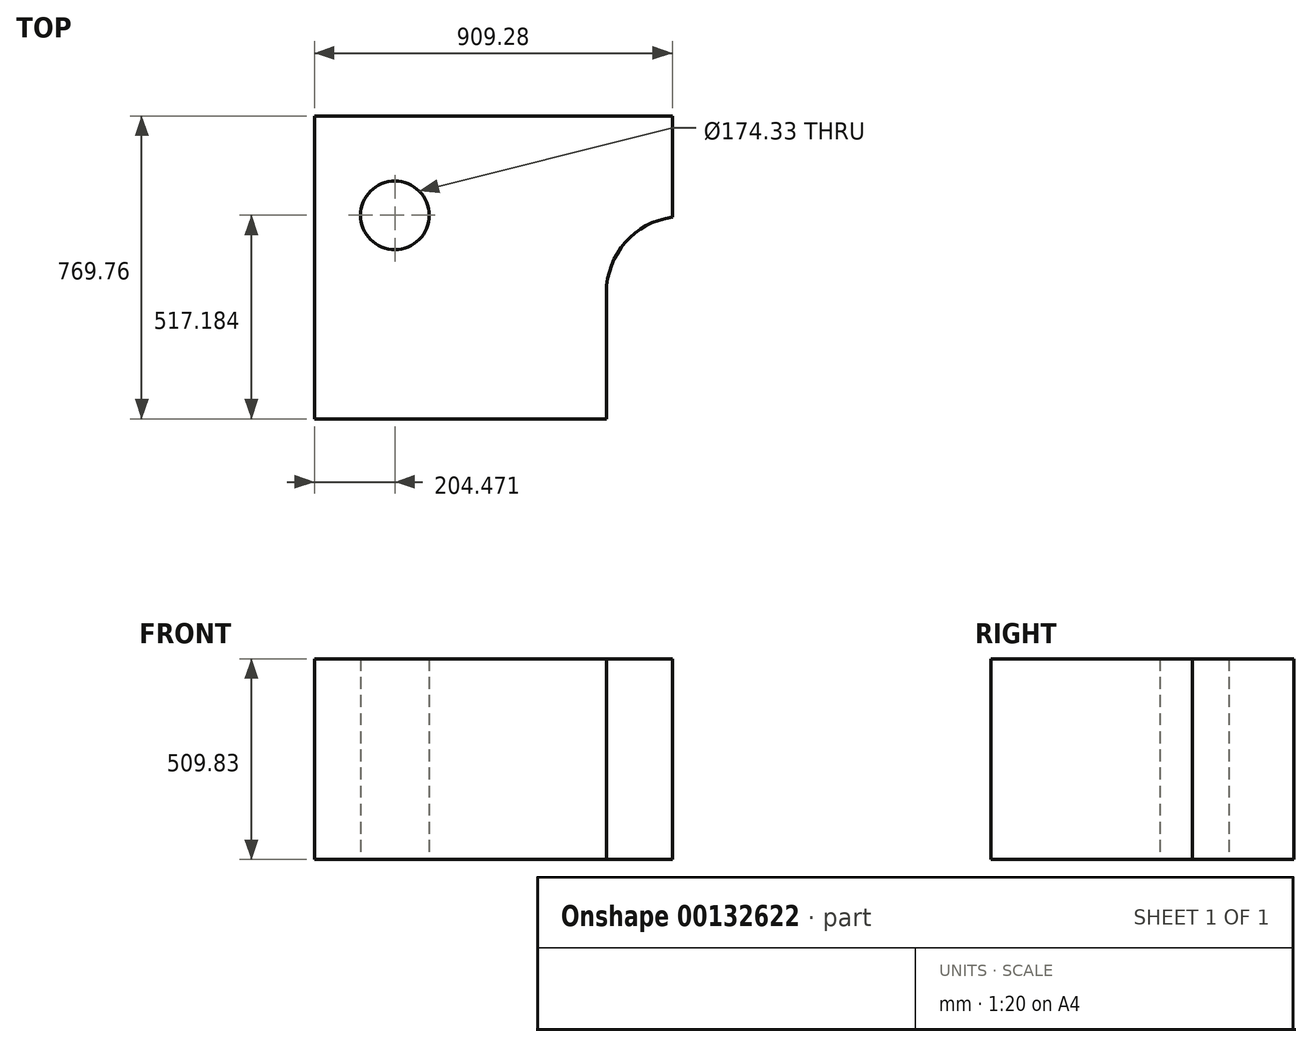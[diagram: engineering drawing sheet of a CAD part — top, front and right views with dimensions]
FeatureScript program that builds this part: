
annotation { "Feature Type Name" : "Feature", "Feature Type Description" : "" }
export const myFeature = defineFeature(function(context is Context, id is Id, definition is map)
    precondition{}
    {
        {
            var Q0;
            Q0=qCreatedBy(makeId("Top.planeOp"),FACE);
            var sketch = newSketch(context, id + "F0", { "sketchPlane" : qUnion([Q0])});
            skLineSegment(sketch, "E0.bottom", {"start": v(-645.88, 306.7) * mm, "end": v(263.4, 306.7) * mm});
            skLineSegment(sketch, "E0.top", {"start": v(-645.88, -463.06) * mm, "end": v(263.4, -463.06) * mm});
            skLineSegment(sketch, "E0.left", {"start": v(-645.88, 306.7) * mm, "end": v(-645.88, -463.06) * mm});
            skLineSegment(sketch, "E0.right", {"start": v(263.4, 306.7) * mm, "end": v(263.4, -463.06) * mm});
            skCircle(sketch, "E1", {"center": v(-441.4, 54.12) * mm, "radius": 87.16 * mm});
            skSolve(sketch);
        }
        {
            var Q0;
            Q0 = qSketchRegion(id + "F0", true);
            extrude(context, id + "F1", {"entities" : qUnion([Q0]), "depth" : 509.83 * mm});
        }
        {
            var Q0;
            Q0=makeQuery(id+"F1.opExtrude","SWEPT_FACE",FACE,{"disambiguationData":[OSD([sQuery(id+"F0.wireOp",EDGE,"E0.right")])]});
            var sketch = newSketch(context, id + "F2", { "sketchPlane" : qUnion([Q0])});
            skLineSegment(sketch, "E2.bottom", {"start": v(-463.06, 509.83) * mm, "end": v(49.12, 509.83) * mm});
            skLineSegment(sketch, "E2.top", {"start": v(-463.06, 0) * mm, "end": v(49.12, 0) * mm});
            skLineSegment(sketch, "E2.left", {"start": v(-463.06, 509.83) * mm, "end": v(-463.06, 0) * mm});
            skLineSegment(sketch, "E2.right", {"start": v(49.12, 509.83) * mm, "end": v(49.12, 0) * mm});
            skSolve(sketch);
        }
        {
            var Q0;
            Q0=makeQuery(id+"F2.imprint","IMPRINT",FACE,{"disambiguationData":[TD([[makeQuery(id+"F2.imprint","IMPRINT",EDGE,{"derivedFrom":sQuery(id+"F2.wireOp",EDGE,"E2.bottom")}),1.0]])]});
            extrude(context, id + "F3", {"entities" : qUnion([Q0]), "operationType" : NewBodyOperationType.REMOVE, "oppositeDirection" : true, "depth" : 167.39 * mm});
        }
        {
            var Q0;
            Q0=makeQuery(id+"F3.boolean.opBoolean","COPY",EDGE,{"derivedFrom":makeQuery(id+"F3.opExtrude","CAP_EDGE",EDGE,{"disambiguationData":[OSD([sQuery(id+"F2.wireOp",EDGE,"E2.right")])],"isStart":false})});
            fillet(context, id + "F4", {"entities" : qUnion([Q0]), "radius" : 192.88 * mm, "tangentPropagation" : true, "allowEdgeOverflow" : false});
        }
    });
